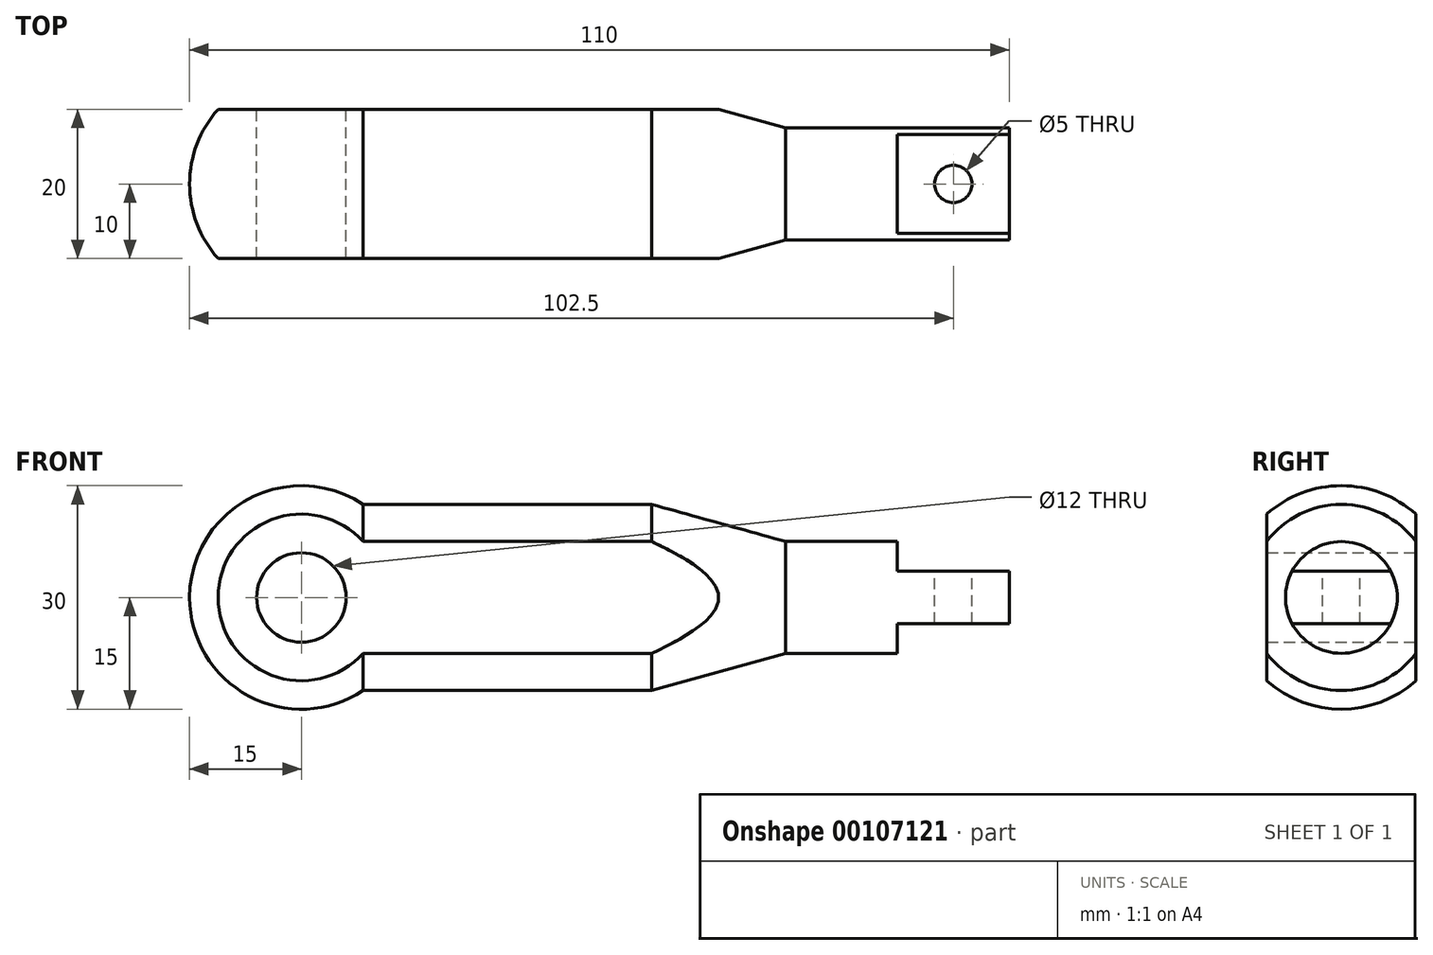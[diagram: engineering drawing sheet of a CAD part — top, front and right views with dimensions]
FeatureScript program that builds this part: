
annotation { "Feature Type Name" : "Feature", "Feature Type Description" : "" }
export const myFeature = defineFeature(function(context is Context, id is Id, definition is map)
    precondition{}
    {
        {
            var Q0;
            Q0=qCreatedBy(makeId("Front.planeOp"),FACE);
            var sketch = newSketch(context, id + "F0", { "sketchPlane" : qUnion([Q0])});
            skArc(sketch, "E0", {"start": v(-15, 0) * mm, "mid": v(-7.1, 13.22) * mm, "end": v(8.3, 12.5) * mm});
            skLineSegment(sketch, "E1", {"start": v(8.3, 12.5) * mm, "end": v(47, 12.5) * mm});
            skLineSegment(sketch, "E2", {"start": v(47, 12.5) * mm, "end": v(65, 7.5) * mm});
            skLineSegment(sketch, "E3", {"start": v(65, 7.5) * mm, "end": v(95, 7.5) * mm});
            skLineSegment(sketch, "E4", {"start": v(95, 7.5) * mm, "end": v(95, 0) * mm});
            skLineSegment(sketch, "E5", {"start": v(95, 0) * mm, "end": v(-15, 0) * mm});
            skLineSegment(sketch, "E6", {"start": v(-23.37, 0) * mm, "end": v(121.6, 0) * mm, "construction": true});
            skSolve(sketch);
        }
        {
            var Q0;
            Q0 = qSketchRegion(id + "F0", true);
            var Q1;
            Q1=sQuery(id+"F0.wireOp",EDGE,"E6");
            revolve(context, id + "F1", {"entities" : qUnion([Q0]), "axis" : qUnion([Q1]), "revolveType" : RevolveType.FULL});
        }
        {
            var Q0;
            Q0=qCreatedBy(makeId("Front.planeOp"),FACE);
            var sketch = newSketch(context, id + "F2", { "sketchPlane" : qUnion([Q0])});
            skLineSegment(sketch, "E7.bottom", {"start": v(95, 7.5) * mm, "end": v(80, 7.5) * mm});
            skLineSegment(sketch, "E7.top", {"start": v(95, 3.5) * mm, "end": v(80, 3.5) * mm});
            skLineSegment(sketch, "E7.left", {"start": v(95, 7.5) * mm, "end": v(95, 3.5) * mm});
            skLineSegment(sketch, "E7.right", {"start": v(80, 7.5) * mm, "end": v(80, 3.5) * mm});
            skLineSegment(sketch, "E8.bottom", {"start": v(95, -7.5) * mm, "end": v(80, -7.5) * mm});
            skLineSegment(sketch, "E8.top", {"start": v(95, -3.5) * mm, "end": v(80, -3.5) * mm});
            skLineSegment(sketch, "E8.left", {"start": v(95, -7.5) * mm, "end": v(95, -3.5) * mm});
            skLineSegment(sketch, "E8.right", {"start": v(80, -7.5) * mm, "end": v(80, -3.5) * mm});
            skSolve(sketch);
        }
        {
            var Q0;
            Q0 = qSketchRegion(id + "F2", true);
            extrude(context, id + "F3", {"entities" : qUnion([Q0]), "operationType" : NewBodyOperationType.REMOVE, "endBound" : BoundingType.SYMMETRIC, "oppositeDirection" : true, "depth" : 15 * mm});
        }
        {
            var Q0;
            Q0=qCreatedBy(makeId("Front.planeOp"),FACE);
            var sketch = newSketch(context, id + "F4", { "sketchPlane" : qUnion([Q0])});
            skCircle(sketch, "E9", {"center": v(0, 0) * mm, "radius": 6 * mm});
            skSolve(sketch);
        }
        {
            var Q0;
            Q0 = qSketchRegion(id + "F4", true);
            extrude(context, id + "F5", {"entities" : qUnion([Q0]), "operationType" : NewBodyOperationType.REMOVE, "endBound" : BoundingType.SYMMETRIC, "depth" : 38.68 * mm});
        }
        {
            var Q0;
            Q0=makeQuery(id+"F1.opRevolve","SWEPT_FACE",FACE,{"disambiguationData":[OSD([sQuery(id+"F0.wireOp",EDGE,"E4")])]});
            var sketch = newSketch(context, id + "F6", { "sketchPlane" : qUnion([Q0])});
            skLineSegment(sketch, "E10", {"start": v(0, 0) * mm, "end": v(10, 0) * mm, "construction": true});
            skPoint(sketch, "E10.endSnap0", {"position": v(7.5, 0) * mm});
            skLineSegment(sketch, "E11", {"start": v(0, 0) * mm, "end": v(-10, 0) * mm, "construction": true});
            skLineSegment(sketch, "E12", {"start": v(10, 0) * mm, "end": v(10, 11.18) * mm});
            skLineSegment(sketch, "E13", {"start": v(10, 0) * mm, "end": v(10, -11.18) * mm});
            skArc(sketch, "E14", {"start": v(10, -11.18) * mm, "mid": v(15, 0) * mm, "end": v(10, 11.18) * mm});
            skLineSegment(sketch, "E15", {"start": v(-10, 0) * mm, "end": v(-10, 11.18) * mm});
            skLineSegment(sketch, "E16", {"start": v(-10, 0) * mm, "end": v(-10, -11.18) * mm});
            skArc(sketch, "E17", {"start": v(-10, 11.18) * mm, "mid": v(-15, 0) * mm, "end": v(-10, -11.18) * mm});
            skSolve(sketch);
        }
        {
            var Q0;
            Q0 = qSketchRegion(id + "F6", true);
            extrude(context, id + "F7", {"entities" : qUnion([Q0]), "operationType" : NewBodyOperationType.REMOVE, "endBound" : BoundingType.THROUGH_ALL, "oppositeDirection" : true, "depth" : 25 * mm});
        }
        {
            var Q0;
            Q0=makeQuery(id+"F3.boolean.opBoolean","COPY",FACE,{"derivedFrom":makeQuery(id+"F3.opExtrude","SWEPT_FACE",FACE,{"disambiguationData":[OSD([sQuery(id+"F2.wireOp",EDGE,"E7.top")])]})});
            var sketch = newSketch(context, id + "F8", { "sketchPlane" : qUnion([Q0])});
            skCircle(sketch, "E18", {"center": v(87.5, 0) * mm, "radius": 2.5 * mm});
            skSolve(sketch);
        }
        {
            var Q0;
            Q0 = qSketchRegion(id + "F8", true);
            extrude(context, id + "F9", {"entities" : qUnion([Q0]), "operationType" : NewBodyOperationType.REMOVE, "endBound" : BoundingType.THROUGH_ALL, "oppositeDirection" : true, "depth" : 25 * mm});
        }
    });
